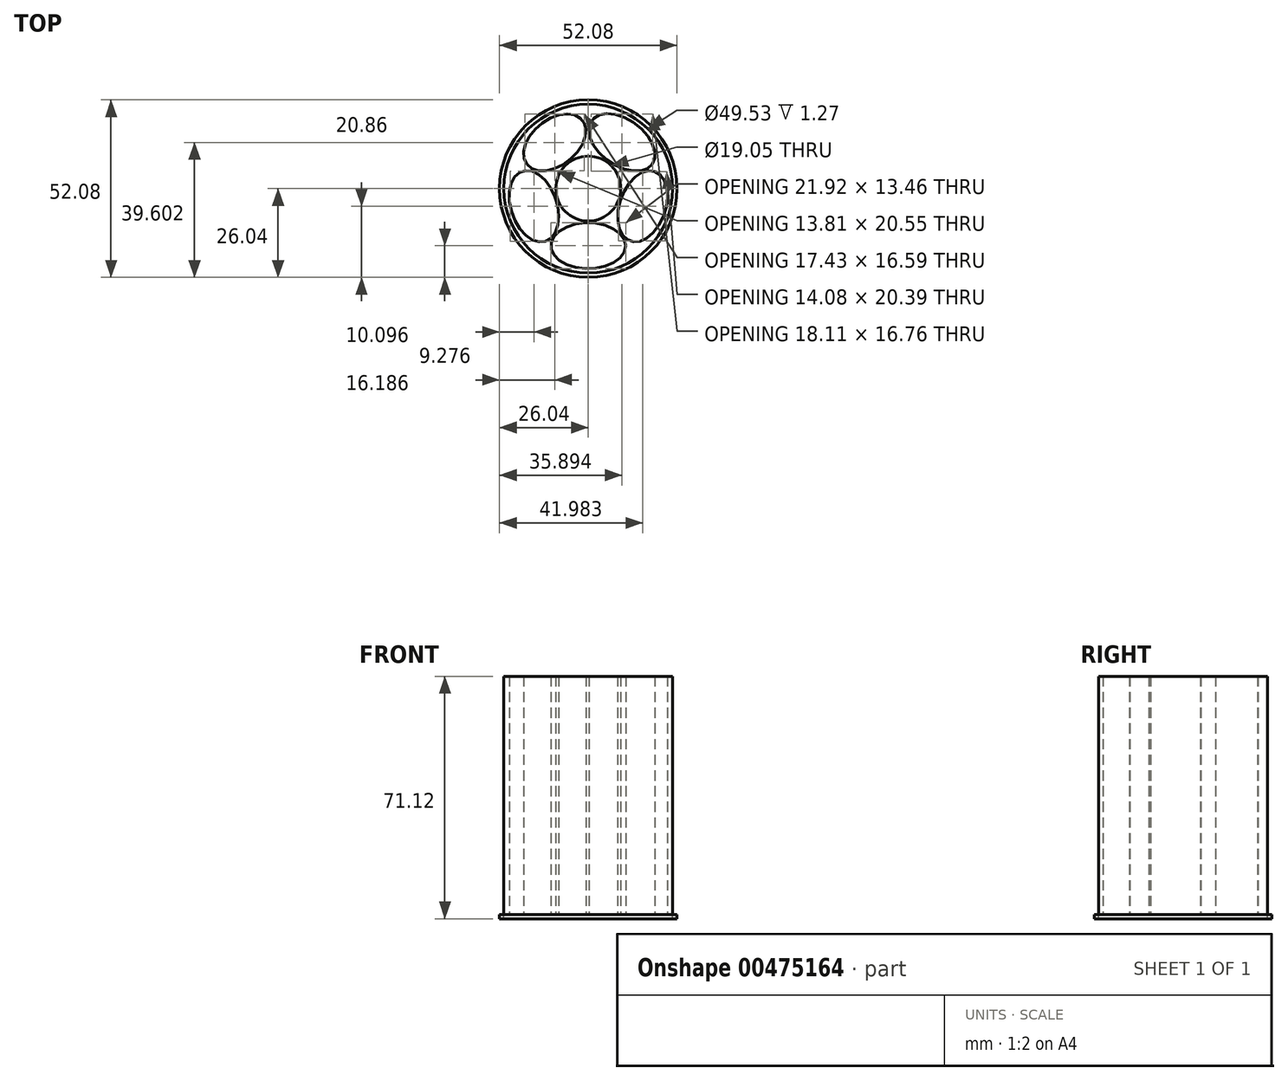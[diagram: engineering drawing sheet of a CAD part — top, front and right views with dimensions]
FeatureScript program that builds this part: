
annotation { "Feature Type Name" : "Feature", "Feature Type Description" : "" }
export const myFeature = defineFeature(function(context is Context, id is Id, definition is map)
    precondition{}
    {
        {
            var Q0;
            Q0=qCreatedBy(makeId("Top.planeOp"),FACE);
            var sketch = newSketch(context, id + "F0", { "sketchPlane" : qUnion([Q0])});
            skCircle(sketch, "E0", {"center": v(0, 0) * mm, "radius": 23.5 * mm});
            skCircle(sketch, "E1", {"center": v(0, 0) * mm, "radius": 10.8 * mm});
            skCircle(sketch, "E2.0", {"center": v(0, 0) * mm, "radius": 24.77 * mm});
            skCircle(sketch, "E3.0", {"center": v(0, 0) * mm, "radius": 9.53 * mm});
            skCircle(sketch, "E4.0", {"center": v(0, 0) * mm, "radius": 26.04 * mm});
            skEllipse(sketch, "E5", {"center": v(9.85, 13.56) * mm, "majorRadius": 10.94 * mm, "minorRadius": 6.72 * mm, "majorAxis": v(0.81, -0.58)});
            skEllipse(sketch, "E6", {"center": v(15.94, -5.18) * mm, "majorRadius": 10.82 * mm, "minorRadius": 6.73 * mm, "majorAxis": v(0.33, 0.94)});
            skEllipse(sketch, "E7", {"center": v(0, -16.76) * mm, "majorRadius": 10.96 * mm, "minorRadius": 6.73 * mm, "majorAxis": v(1, 0)});
            skEllipse(sketch, "E8", {"center": v(-9.85, 13.56) * mm, "majorRadius": 10.4 * mm, "minorRadius": 6.73 * mm, "majorAxis": v(-0.78, -0.62)});
            skEllipse(sketch, "E9", {"center": v(-15.94, -5.18) * mm, "majorRadius": 10.81 * mm, "minorRadius": 6.73 * mm, "majorAxis": v(0.31, -0.95)});
            skSolve(sketch);
        }
        {
            var Q0;
            Q0=makeQuery(id+"F0.imprint","IMPRINT",FACE,{"disambiguationData":[TD([[makeQuery(id+"F0.imprint","IMPRINT",EDGE,{"derivedFrom":sQuery(id+"F0.wireOp",EDGE,"E2.0")}),1.0]])]});
            var Q1;
            {var subQ0=sQuery(id+"F0.wireOp",EDGE,"E9");var subQ1=sQuery(id+"F0.wireOp",EDGE,"E0");var subQ2=makeQuery(id+"F0.imprint","INTERSECT",VERTEX,{"disambiguationData":[OD(1.0)],"derivedFrom":[subQ1,subQ0]});Q1=makeQuery(id+"F0.imprint","IMPRINT",FACE,{"disambiguationData":[TD([[makeQuery(id+"F0.imprint","IMPRINT",EDGE,{"disambiguationData":[TD([[subQ2,-1.0]])],"derivedFrom":subQ1}),1.0]])]});}
            var Q2;
            {var subQ0=sQuery(id+"F0.wireOp",EDGE,"E7");var subQ1=sQuery(id+"F0.wireOp",EDGE,"E0");var subQ2=makeQuery(id+"F0.imprint","INTERSECT",VERTEX,{"derivedFrom":[subQ1,subQ0]});Q2=makeQuery(id+"F0.imprint","IMPRINT",FACE,{"disambiguationData":[TD([[makeQuery(id+"F0.imprint","IMPRINT",EDGE,{"disambiguationData":[TD([[subQ2,-1.0]])],"derivedFrom":subQ1}),1.0]])]});}
            var Q3;
            Q3=makeQuery(id+"F0.imprint","IMPRINT",FACE,{"disambiguationData":[TD([[makeQuery(id+"F0.imprint","IMPRINT",EDGE,{"derivedFrom":sQuery(id+"F0.wireOp",EDGE,"E3.0")}),-1.0]])]});
            var Q4;
            Q4=makeQuery(id+"F0.imprint","IMPRINT",FACE,{"disambiguationData":[TD([[makeQuery(id+"F0.imprint","IMPRINT",EDGE,{"derivedFrom":sQuery(id+"F0.wireOp",EDGE,"E5")}),-1.0]])]});
            var Q5;
            {var subQ0=sQuery(id+"F0.wireOp",EDGE,"E9");var subQ1=sQuery(id+"F0.wireOp",EDGE,"E0");var subQ2=makeQuery(id+"F0.imprint","INTERSECT",VERTEX,{"disambiguationData":[OD(0.0)],"derivedFrom":[subQ1,subQ0]});Q5=makeQuery(id+"F0.imprint","IMPRINT",FACE,{"disambiguationData":[TD([[makeQuery(id+"F0.imprint","IMPRINT",EDGE,{"disambiguationData":[TD([[subQ2,1.0]])],"derivedFrom":subQ1}),1.0]])]});}
            extrude(context, id + "F1", {"entities" : qUnion([Q0, Q1, Q2, Q3, Q4, Q5]), "depth" : 69.85 * mm});
        }
        {
            var Q0;
            Q0=makeQuery(id+"F0.imprint","IMPRINT",FACE,{"disambiguationData":[TD([[makeQuery(id+"F0.imprint","IMPRINT",EDGE,{"derivedFrom":sQuery(id+"F0.wireOp",EDGE,"E2.0")}),-1.0]])]});
            extrude(context, id + "F2", {"entities" : qUnion([Q0]), "oppositeDirection" : true, "depth" : 1.27 * mm});
        }
    });
